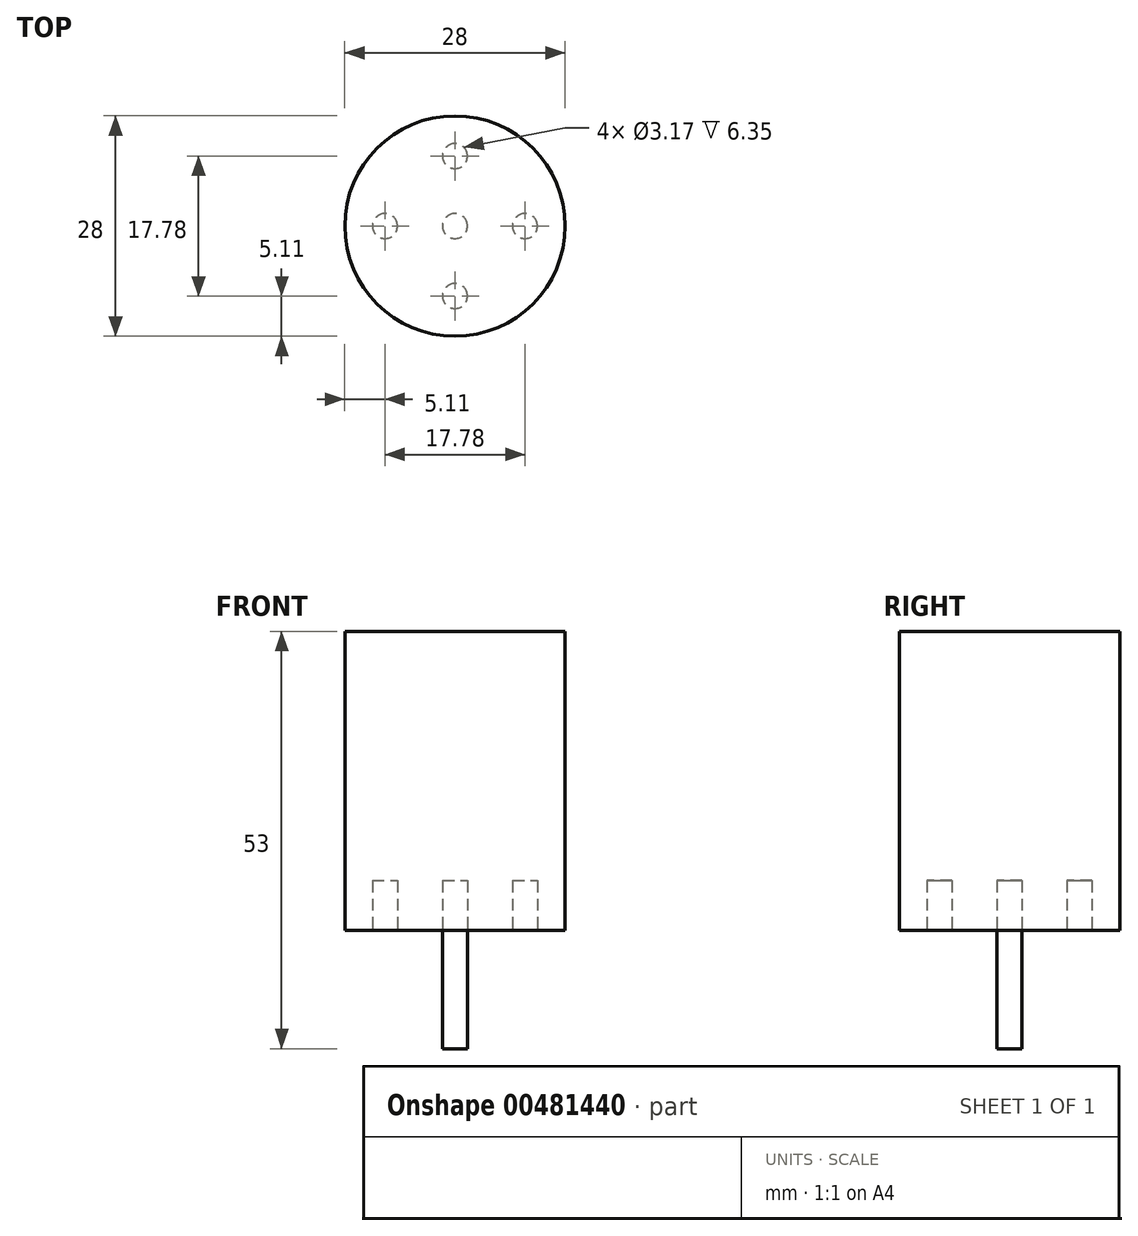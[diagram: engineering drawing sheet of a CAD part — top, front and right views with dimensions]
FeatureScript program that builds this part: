
annotation { "Feature Type Name" : "Feature", "Feature Type Description" : "" }
export const myFeature = defineFeature(function(context is Context, id is Id, definition is map)
    precondition{}
    {
        {
            var Q0;
            Q0=qCreatedBy(makeId("Front.planeOp"),FACE);
            var sketch = newSketch(context, id + "F0", { "sketchPlane" : qUnion([Q0])});
            skLineSegment(sketch, "E0", {"start": v(0, 0) * mm, "end": v(0, 69.27) * mm, "construction": true});
            skLineSegment(sketch, "E1", {"start": v(0, 0) * mm, "end": v(1.59, 0) * mm});
            skLineSegment(sketch, "E2", {"start": v(1.59, 0) * mm, "end": v(1.59, 15) * mm});
            skLineSegment(sketch, "E3", {"start": v(1.59, 15) * mm, "end": v(14, 15) * mm});
            skLineSegment(sketch, "E4", {"start": v(14, 15) * mm, "end": v(14, 53) * mm});
            skLineSegment(sketch, "E5", {"start": v(14, 53) * mm, "end": v(0, 53) * mm});
            skLineSegment(sketch, "E6", {"start": v(0, 53) * mm, "end": v(0, 0) * mm});
            skSolve(sketch);
        }
        {
            var Q0;
            Q0 = qSketchRegion(id + "F0", true);
            var Q1;
            Q1=sQuery(id+"F0.wireOp",EDGE,"E0");
            revolve(context, id + "F1", {"entities" : qUnion([Q0]), "axis" : qUnion([Q1]), "revolveType" : RevolveType.FULL});
        }
        {
            var Q0;
            Q0=makeQuery(id+"F1.opRevolve","SWEPT_FACE",FACE,{"disambiguationData":[OSD([sQuery(id+"F0.wireOp",EDGE,"E3")])]});
            var sketch = newSketch(context, id + "F2", { "sketchPlane" : qUnion([Q0])});
            skLineSegment(sketch, "E7", {"start": v(-20.4, 0) * mm, "end": v(21.36, 0) * mm, "construction": true});
            skLineSegment(sketch, "E8", {"start": v(0, 17.3) * mm, "end": v(0, -18.33) * mm, "construction": true});
            skCircle(sketch, "E9", {"center": v(8.9, 0) * mm, "radius": 1.59 * mm});
            skCircle(sketch, "E10", {"center": v(0, 8.9) * mm, "radius": 1.59 * mm});
            skCircle(sketch, "E11.MirrorC", {"center": v(0, -8.9) * mm, "radius": 1.59 * mm});
            skCircle(sketch, "E12.MirrorC", {"center": v(-8.89, 0) * mm, "radius": 1.59 * mm});
            skSolve(sketch);
        }
        {
            var Q0;
            Q0 = qSketchRegion(id + "F2", true);
            extrude(context, id + "F3", {"entities" : qUnion([Q0]), "operationType" : NewBodyOperationType.REMOVE, "oppositeDirection" : true, "depth" : 6.35 * mm});
        }
    });
